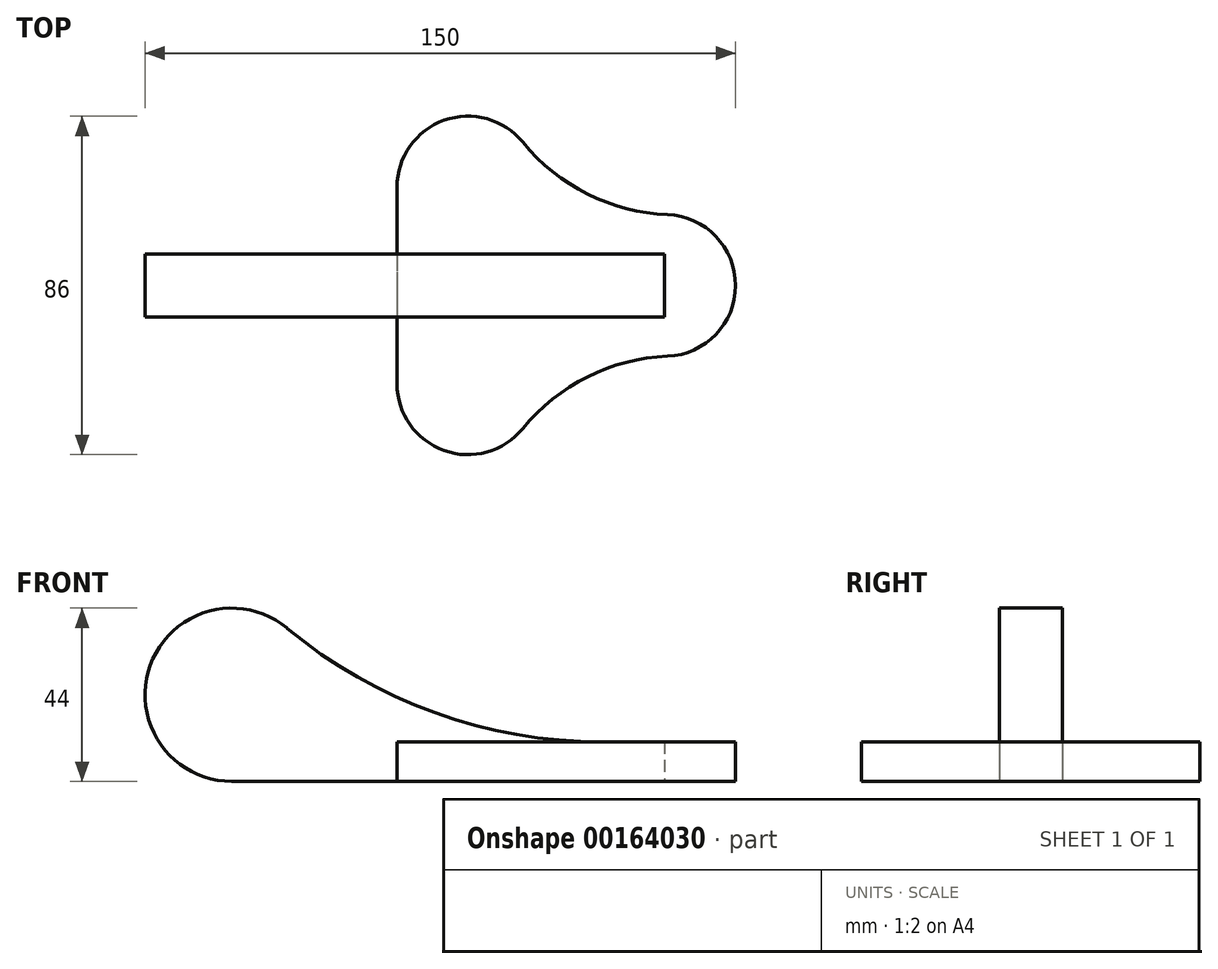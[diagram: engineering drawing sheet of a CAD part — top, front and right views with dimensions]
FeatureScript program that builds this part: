
annotation { "Feature Type Name" : "Feature", "Feature Type Description" : "" }
export const myFeature = defineFeature(function(context is Context, id is Id, definition is map)
    precondition{}
    {
        {
            var Q0;
            Q0=qCreatedBy(makeId("Top.planeOp"),FACE);
            var sketch = newSketch(context, id + "F0", { "sketchPlane" : qUnion([Q0])});
            skArc(sketch, "E0", {"start": v(-36.04, 36.37) * mm, "mid": v(-56.03, 41.96) * mm, "end": v(-68, 25) * mm});
            skArc(sketch, "E1", {"start": v(-68, -25) * mm, "mid": v(-56.03, -41.96) * mm, "end": v(-36.04, -36.37) * mm});
            skArc(sketch, "E2", {"start": v(0.72, -17.99) * mm, "mid": v(18, 0) * mm, "end": v(0.72, 17.99) * mm});
            skLineSegment(sketch, "E3", {"start": v(-68, 25) * mm, "end": v(-68, -25) * mm});
            skArc(sketch, "E4", {"start": v(0.72, -17.99) * mm, "mid": v(-19.64, -23.22) * mm, "end": v(-36.04, -36.37) * mm});
            skArc(sketch, "E5", {"start": v(-36.04, 36.37) * mm, "mid": v(-19.64, 23.22) * mm, "end": v(0.72, 17.99) * mm});
            skSolve(sketch);
        }
        {
            var Q0;
            Q0=qCreatedBy(makeId("Front.planeOp"),FACE);
            var sketch = newSketch(context, id + "F1", { "sketchPlane" : qUnion([Q0])});
            skArc(sketch, "E6", {"start": v(-95.93, 38.91) * mm, "mid": v(-130.69, 29.48) * mm, "end": v(-110, 0) * mm});
            skLineSegment(sketch, "E7", {"start": v(-110, 0) * mm, "end": v(0, 0) * mm});
            skLineSegment(sketch, "E8", {"start": v(-15.98, 10) * mm, "end": v(0, 10) * mm});
            skLineSegment(sketch, "E9", {"start": v(0, 10) * mm, "end": v(0, 0) * mm});
            skArc(sketch, "E10", {"start": v(-95.93, 38.91) * mm, "mid": v(-58.49, 17.45) * mm, "end": v(-15.98, 10) * mm});
            skPoint(sketch, "E11.orphan", {"position": v(35.39, 0) * mm});
            skPoint(sketch, "E12.orphan", {"position": v(-47.1, 10) * mm});
            skSolve(sketch);
        }
        {
            var Q0;
            Q0=makeQuery(id+"F0.imprint","IMPRINT",FACE,{"disambiguationData":[TD([[makeQuery(id+"F0.imprint","IMPRINT",EDGE,{"derivedFrom":sQuery(id+"F0.wireOp",EDGE,"E0")}),1.0]])]});
            extrude(context, id + "F2", {"entities" : qUnion([Q0]), "depth" : 10 * mm});
        }
        {
            var Q0;
            {var subQ2=sQuery(id+"F1.wireOp",EDGE,"E6");Q0=makeQuery(id+"F1.imprint","IMPRINT",FACE,{"disambiguationData":[TD([[makeQuery(id+"F1.imprint","IMPRINT",EDGE,{"derivedFrom":subQ2}),1.0]])]});}
            extrude(context, id + "F3", {"entities" : qUnion([Q0]), "endBound" : BoundingType.SYMMETRIC, "depth" : 16 * mm});
        }
    });
